FCSTD DOCUMENT  (FreeCAD 0.20R29410 (Git))
Label: TrainConnectorSketch0
License: All rights reserved
LicenseURL: http://en.wikipedia.org/wiki/All_rights_reserved
objects: Sketcher::SketchObject×1
note: 1 computed .brp shape members not serialized (recipe doc carries the construction recipe); baked Part::Feature solids carry a one-line shape summary decoded from their .brp

FEATURE [Sketcher::SketchObject] Sketch
  FullyConstrained = false
  sketch-geometry (16):
    g0: LineSegment StartX=-8.48528 StartY=0 StartZ=0 EndX=0 EndY=8.48528 EndZ=0
    g1: LineSegment StartX=0 StartY=8.48528 StartZ=0 EndX=0 EndY=20 EndZ=0
    g2: LineSegment StartX=0 StartY=20 StartZ=0 EndX=-28.4853 EndY=20 EndZ=0
    g3: LineSegment StartX=-28.4853 StartY=20 StartZ=0 EndX=-8.48528 EndY=0 EndZ=0
    g4: LineSegment StartX=-24.9112 StartY=-18.5473 StartZ=0 EndX=-3.6e-15 EndY=6.36396 EndZ=0
    g5: LineSegment StartX=-8.48528 StartY=0 StartZ=0 EndX=-7.42462 EndY=-1.06066 EndZ=0
    g6: GeomPoint X=-15.2028 Y=6.71751 Z=0
    g7: LineSegment StartX=-15.2028 StartY=6.71751 StartZ=0 EndX=7.77246 EndY=29.6928 EndZ=0
    g8: LineSegment StartX=-18.0489 StartY=9.56362 StartZ=0 EndX=1.86323 EndY=29.4758 EndZ=0
    g9: LineSegment StartX=-12.3567 StartY=3.87141 StartZ=0 EndX=6.87214 EndY=23.1002 EndZ=0
    g10: LineSegment StartX=-15.2028 StartY=6.71751 StartZ=0 EndX=-15.9099 EndY=6.01041 EndZ=0
    g11: LineSegment StartX=-23.6881 StartY=13.7886 StartZ=0 EndX=-8.13173 EndY=-1.76777 EndZ=0
    g12: LineSegment StartX=-8.13173 StartY=-1.76777 StartZ=0 EndX=-13.0815 EndY=-6.71751 EndZ=0
    g13: LineSegment StartX=-13.0815 StartY=-6.71751 StartZ=0 EndX=-28.6378 EndY=8.83883 EndZ=0
    g14: LineSegment StartX=-28.6378 StartY=8.83883 StartZ=0 EndX=-23.6881 EndY=13.7886 EndZ=0
    g15: GeomPoint X=-10.6066 Y=-4.24264 Z=0
  constraints (46):
    c: PointOnObject(g0,g-1)
    c: PointOnObject(g0,g-2)
    c: Angle(g0,g-2) = 0.785398
    c: Coincident(g1,g0)
    c: PointOnObject(g1,g-2)
    c: Coincident(g2,g1)
    c: Horizontal(g2)
    c: Coincident(g3,g2)
    c: Coincident(g3,g0)
    c: Perpendicular(g0,g3)
    c: DistanceY(g-1,g1) = 20
    c: Parallel(g4,g0)
    c: PointOnObject(g4,g-2)
    c: Coincident(g5,g0)
    c: PointOnObject(g5,g4)
    c: Perpendicular(g4,g5)
    c: Distance(g0,g5) = 1.5
    c: PointOnObject(g6,g3)
    c: Coincident(g7,g6)
    c: Perpendicular(g3,g7)
    c: Distance(g5,g6) = 11
    c: PointOnObject(g8,g3)
    c: Parallel(g8,g7)
    c: Parallel(g8,g9)
    c: Symmetric(g8,g9,g7)
    c: Distance(g9,g8) = 8.05
    c: Coincident(g10,g6)
    c: Parallel(g10,g7)
    c: Distance(g10,g6) = 1
    c: PointOnObject(g11,g4)
    c: Coincident(g11,g12)
    c: PointOnObject(g12,g4)
    c: Coincident(g12,g13)
    c: Coincident(g13,g14)
    c: Coincident(g14,g11)
    c: Perpendicular(g14,g11)
    c: Perpendicular(g13,g14)
    c: Perpendicular(g13,g12)
    c: Distance(g11,g13) = 7
    c: Distance(g12,g13) = 22
    c: PointOnObject(g10,g11)
    c: Symmetric(g11,g12,g15)
    c: Distance(g4,g15) = 15
    c: Distance(g2) = 28.4853
    c: Distance(g1) = 11.5147
    c: Distance(g3) = 28.2843
